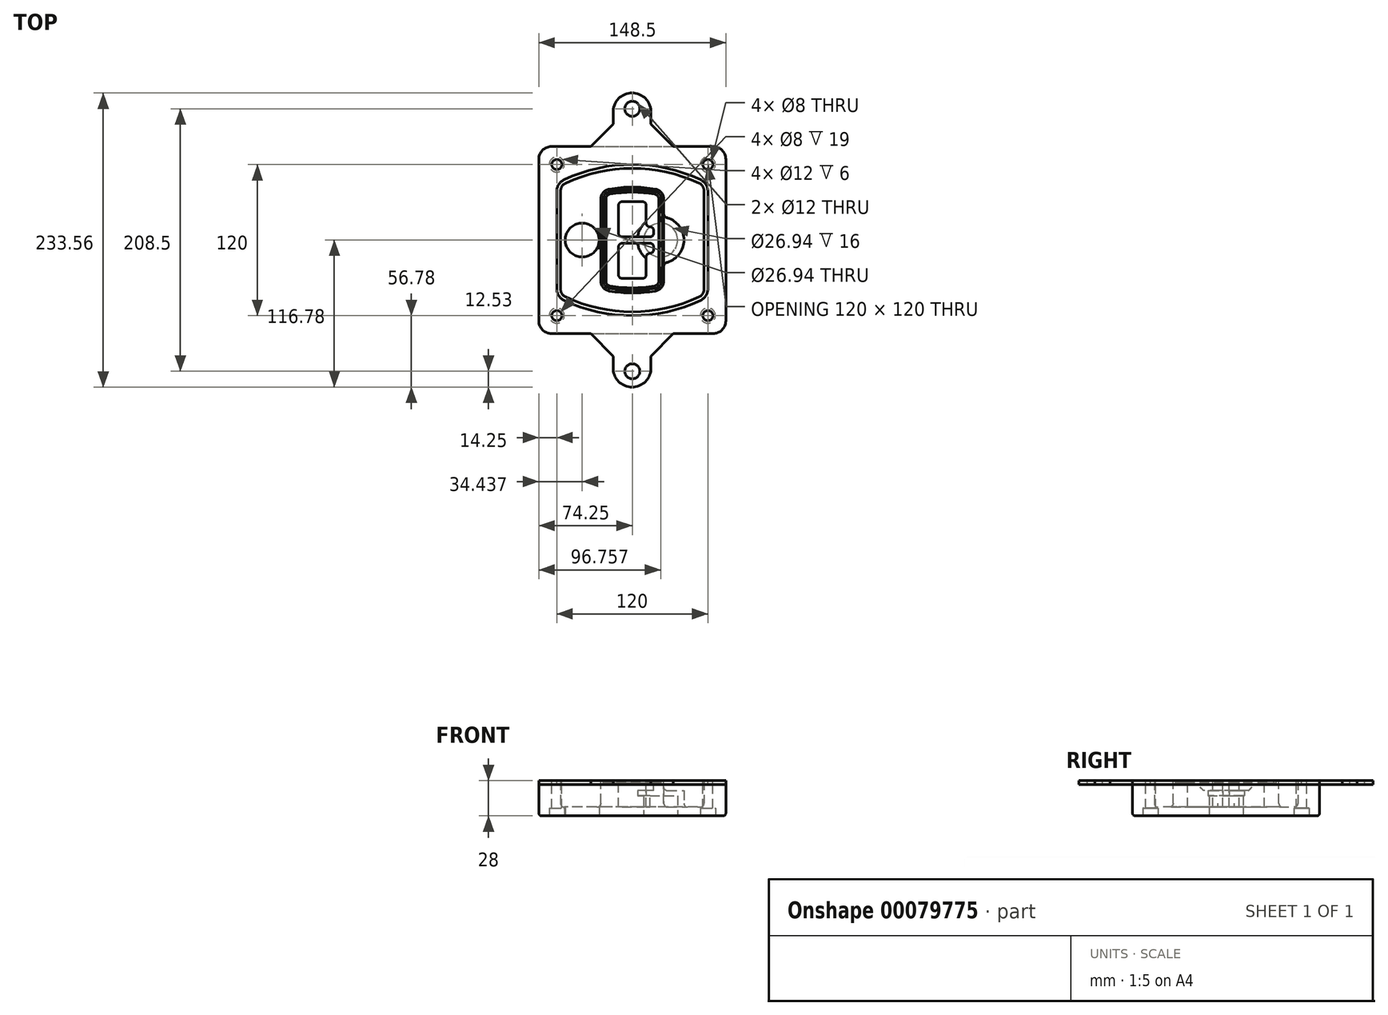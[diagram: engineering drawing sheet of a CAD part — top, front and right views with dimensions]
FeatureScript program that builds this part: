
annotation { "Feature Type Name" : "Feature", "Feature Type Description" : "" }
export const myFeature = defineFeature(function(context is Context, id is Id, definition is map)
    precondition{}
    {
        {
            var Q0;
            Q0=qCreatedBy(makeId("Top.planeOp"),FACE);
            var sketch = newSketch(context, id + "F0", { "sketchPlane" : qUnion([Q0])});
            skPoint(sketch, "E0.rect.middle", {"position": v(0, 0) * mm});
            skLineSegment(sketch, "E1.bottom", {"start": v(-64.25, -74.25) * mm, "end": v(64.25, -74.25) * mm});
            skLineSegment(sketch, "E1.top", {"start": v(-64.25, 74.25) * mm, "end": v(64.25, 74.25) * mm});
            skLineSegment(sketch, "E1.left", {"start": v(-74.25, -64.25) * mm, "end": v(-74.25, 64.25) * mm});
            skLineSegment(sketch, "E1.right", {"start": v(74.25, -64.25) * mm, "end": v(74.25, 64.25) * mm});
            skLineSegment(sketch, "E2", {"start": v(-74.25, 74.25) * mm, "end": v(74.25, -74.25) * mm, "construction": true});
            skLineSegment(sketch, "E3", {"start": v(74.25, 74.25) * mm, "end": v(-74.25, -74.25) * mm, "construction": true});
            skCircle(sketch, "E4", {"center": v(-60, 60) * mm, "radius": 4 * mm});
            skCircle(sketch, "E5", {"center": v(60, 60) * mm, "radius": 4 * mm});
            skCircle(sketch, "E6", {"center": v(60, -60) * mm, "radius": 4 * mm});
            skCircle(sketch, "E7", {"center": v(-60, -60) * mm, "radius": 4 * mm});
            skLineSegment(sketch, "E8", {"start": v(-60, 60) * mm, "end": v(60, 60) * mm, "construction": true});
            skLineSegment(sketch, "E9", {"start": v(60, 60) * mm, "end": v(60, -60) * mm, "construction": true});
            skLineSegment(sketch, "E10", {"start": v(60, -60) * mm, "end": v(-60, -60) * mm, "construction": true});
            skLineSegment(sketch, "E11", {"start": v(-60, -60) * mm, "end": v(-60, 60) * mm, "construction": true});
            skLineSegment(sketch, "E12", {"start": v(-60, 38.83) * mm, "end": v(-60, -38.83) * mm});
            skLineSegment(sketch, "E13", {"start": v(60, 38.83) * mm, "end": v(60, -38.83) * mm});
            skArc(sketch, "E14", {"start": v(54.26, 47.88) * mm, "mid": v(0, 60) * mm, "end": v(-54.26, 47.88) * mm});
            skArc(sketch, "E15", {"start": v(-54.26, -47.88) * mm, "mid": v(0, -60) * mm, "end": v(54.26, -47.88) * mm});
            skLineSegment(sketch, "E16", {"start": v(-60, 0) * mm, "end": v(60, 0) * mm, "construction": true});
            skPoint(sketch, "E17.visualSharp", {"position": v(-60, -45) * mm});
            skArc(sketch, "E17.filletArc", {"start": v(-60, -38.83) * mm, "mid": v(-58.44, -44.2) * mm, "end": v(-54.26, -47.88) * mm});
            skPoint(sketch, "E18.visualSharp", {"position": v(-60, 45) * mm});
            skArc(sketch, "E18.filletArc", {"start": v(-54.26, 47.88) * mm, "mid": v(-58.44, 44.2) * mm, "end": v(-60, 38.83) * mm});
            skPoint(sketch, "E19.visualSharp", {"position": v(60, 45) * mm});
            skArc(sketch, "E19.filletArc", {"start": v(60, 38.83) * mm, "mid": v(58.44, 44.2) * mm, "end": v(54.26, 47.88) * mm});
            skPoint(sketch, "E20.visualSharp", {"position": v(60, -45) * mm});
            skArc(sketch, "E20.filletArc", {"start": v(54.26, -47.88) * mm, "mid": v(58.44, -44.2) * mm, "end": v(60, -38.83) * mm});
            skPoint(sketch, "E21.visualSharp", {"position": v(-74.25, 74.25) * mm});
            skArc(sketch, "E21.filletArc", {"start": v(-64.25, 74.25) * mm, "mid": v(-71.32, 71.32) * mm, "end": v(-74.25, 64.25) * mm});
            skPoint(sketch, "E22.visualSharp", {"position": v(74.25, 74.25) * mm});
            skArc(sketch, "E22.filletArc", {"start": v(74.25, 64.25) * mm, "mid": v(71.32, 71.32) * mm, "end": v(64.25, 74.25) * mm});
            skPoint(sketch, "E23.visualSharp", {"position": v(74.25, -74.25) * mm});
            skArc(sketch, "E23.filletArc", {"start": v(64.25, -74.25) * mm, "mid": v(71.32, -71.32) * mm, "end": v(74.25, -64.25) * mm});
            skPoint(sketch, "E24.visualSharp", {"position": v(-74.25, -74.25) * mm});
            skArc(sketch, "E24.filletArc", {"start": v(-74.25, -64.25) * mm, "mid": v(-71.32, -71.32) * mm, "end": v(-64.25, -74.25) * mm});
            skArc(sketch, "E25.0", {"start": v(57, 38.83) * mm, "mid": v(55.9, 42.58) * mm, "end": v(52.98, 45.17) * mm});
            skLineSegment(sketch, "E25.1", {"start": v(57, 38.83) * mm, "end": v(57, -38.83) * mm});
            skArc(sketch, "E25.2", {"start": v(52.98, -45.17) * mm, "mid": v(55.9, -42.58) * mm, "end": v(57, -38.83) * mm});
            skArc(sketch, "E25.3", {"start": v(-52.98, -45.17) * mm, "mid": v(0, -57) * mm, "end": v(52.98, -45.17) * mm});
            skArc(sketch, "E25.4", {"start": v(-57, -38.83) * mm, "mid": v(-55.9, -42.58) * mm, "end": v(-52.98, -45.17) * mm});
            skArc(sketch, "E25.5", {"start": v(52.98, 45.17) * mm, "mid": v(0, 57) * mm, "end": v(-52.98, 45.17) * mm});
            skLineSegment(sketch, "E25.6", {"start": v(-57, 38.83) * mm, "end": v(-57, -38.83) * mm});
            skArc(sketch, "E25.7", {"start": v(-52.98, 45.17) * mm, "mid": v(-55.9, 42.58) * mm, "end": v(-57, 38.83) * mm});
            skArc(sketch, "E26.0", {"start": v(-55.96, 51.5) * mm, "mid": v(-61.82, 46.33) * mm, "end": v(-64, 38.83) * mm});
            skArc(sketch, "E26.1", {"start": v(55.96, 51.5) * mm, "mid": v(0, 64) * mm, "end": v(-55.96, 51.5) * mm});
            skArc(sketch, "E26.2", {"start": v(64, 38.83) * mm, "mid": v(61.82, 46.33) * mm, "end": v(55.96, 51.5) * mm});
            skLineSegment(sketch, "E26.3", {"start": v(64, 38.83) * mm, "end": v(64, -38.83) * mm});
            skArc(sketch, "E26.4", {"start": v(55.96, -51.5) * mm, "mid": v(61.82, -46.33) * mm, "end": v(64, -38.83) * mm});
            skLineSegment(sketch, "E26.5", {"start": v(-64, 38.83) * mm, "end": v(-64, -38.83) * mm});
            skArc(sketch, "E26.6", {"start": v(-55.96, -51.5) * mm, "mid": v(0, -64) * mm, "end": v(55.96, -51.5) * mm});
            skArc(sketch, "E26.7", {"start": v(-64, -38.83) * mm, "mid": v(-61.82, -46.33) * mm, "end": v(-55.96, -51.5) * mm});
            skSolve(sketch);
        }
        {
            var Q0;
            Q0=makeQuery(id+"F0.imprint","IMPRINT",FACE,{"disambiguationData":[TD([[makeQuery(id+"F0.imprint","IMPRINT",EDGE,{"derivedFrom":sQuery(id+"F0.wireOp",EDGE,"E1.bottom")}),1.0]])]});
            var Q1;
            Q1=makeQuery(id+"F0.imprint","IMPRINT",FACE,{"disambiguationData":[TD([[makeQuery(id+"F0.imprint","IMPRINT",EDGE,{"derivedFrom":sQuery(id+"F0.wireOp",EDGE,"E12")}),1.0]])]});
            var Q2;
            Q2=makeQuery(id+"F0.imprint","IMPRINT",FACE,{"disambiguationData":[TD([[makeQuery(id+"F0.imprint","IMPRINT",EDGE,{"derivedFrom":sQuery(id+"F0.wireOp",EDGE,"E25.0")}),1.0]])]});
            var Q3;
            Q3=makeQuery(id+"F0.imprint","IMPRINT",FACE,{"disambiguationData":[TD([[makeQuery(id+"F0.imprint","IMPRINT",EDGE,{"derivedFrom":sQuery(id+"F0.wireOp",EDGE,"E12")}),-1.0]])]});
            extrude(context, id + "F1", {"entities" : qUnion([Q0, Q1, Q2, Q3]), "oppositeDirection" : true, "depth" : 25 * mm});
        }
        {
            var Q0;
            Q0=makeQuery(id+"F0.imprint","IMPRINT",FACE,{"disambiguationData":[TD([[makeQuery(id+"F0.imprint","IMPRINT",EDGE,{"derivedFrom":sQuery(id+"F0.wireOp",EDGE,"E12")}),1.0]])]});
            extrude(context, id + "F2", {"entities" : qUnion([Q0]), "operationType" : NewBodyOperationType.ADD, "depth" : 3 * mm});
        }
        {
            var Q0;
            Q0=makeQuery(id+"F0.imprint","IMPRINT",FACE,{"disambiguationData":[TD([[makeQuery(id+"F0.imprint","IMPRINT",EDGE,{"derivedFrom":sQuery(id+"F0.wireOp",EDGE,"E25.0")}),1.0]])]});
            extrude(context, id + "F3", {"entities" : qUnion([Q0]), "operationType" : NewBodyOperationType.REMOVE, "oppositeDirection" : true, "depth" : 18 * mm});
        }
        {
            var Q0;
            Q0=makeQuery(id+"F2.opExtrude","CAP_FACE",FACE,{"disambiguationData":[OSD([sQuery(id+"F0.wireOp",EDGE,"E12"),sQuery(id+"F0.wireOp",EDGE,"E13"),sQuery(id+"F0.wireOp",EDGE,"E14"),sQuery(id+"F0.wireOp",EDGE,"E15"),sQuery(id+"F0.wireOp",EDGE,"E17.filletArc"),sQuery(id+"F0.wireOp",EDGE,"E18.filletArc"),sQuery(id+"F0.wireOp",EDGE,"E19.filletArc"),sQuery(id+"F0.wireOp",EDGE,"E20.filletArc"),sQuery(id+"F0.wireOp",EDGE,"E25.0"),sQuery(id+"F0.wireOp",EDGE,"E25.1"),sQuery(id+"F0.wireOp",EDGE,"E25.2"),sQuery(id+"F0.wireOp",EDGE,"E25.3"),sQuery(id+"F0.wireOp",EDGE,"E25.4"),sQuery(id+"F0.wireOp",EDGE,"E25.5"),sQuery(id+"F0.wireOp",EDGE,"E25.6"),sQuery(id+"F0.wireOp",EDGE,"E25.7")])],"isStart":false});
            var sketch = newSketch(context, id + "F4", { "sketchPlane" : qUnion([Q0])});
            skArc(sketch, "E27.0", {"start": v(-18.34, -40.45) * mm, "mid": v(0, -42) * mm, "end": v(18.34, -40.45) * mm});
            skArc(sketch, "E28.0", {"start": v(18.34, 40.45) * mm, "mid": v(0, 42) * mm, "end": v(-18.34, 40.45) * mm});
            skLineSegment(sketch, "E29", {"start": v(-25, 32.57) * mm, "end": v(-25, -32.57) * mm});
            skLineSegment(sketch, "E30", {"start": v(25, 32.57) * mm, "end": v(25, -32.57) * mm});
            skLineSegment(sketch, "E31", {"start": v(-25, 39.1) * mm, "end": v(25, 39.1) * mm, "construction": true});
            skLineSegment(sketch, "E32", {"start": v(-25, -39.1) * mm, "end": v(25, -39.1) * mm, "construction": true});
            skPoint(sketch, "E33.visualSharp", {"position": v(-25, 39.1) * mm});
            skArc(sketch, "E33.filletArc", {"start": v(-18.34, 40.45) * mm, "mid": v(-23.11, 37.73) * mm, "end": v(-25, 32.57) * mm});
            skPoint(sketch, "E34.visualSharp", {"position": v(25, 39.1) * mm});
            skArc(sketch, "E34.filletArc", {"start": v(25, 32.57) * mm, "mid": v(23.11, 37.73) * mm, "end": v(18.34, 40.45) * mm});
            skPoint(sketch, "E35.visualSharp", {"position": v(25, -39.1) * mm});
            skArc(sketch, "E35.filletArc", {"start": v(18.34, -40.45) * mm, "mid": v(23.11, -37.73) * mm, "end": v(25, -32.57) * mm});
            skPoint(sketch, "E36.visualSharp", {"position": v(-25, -39.1) * mm});
            skArc(sketch, "E36.filletArc", {"start": v(-25, -32.57) * mm, "mid": v(-23.11, -37.73) * mm, "end": v(-18.34, -40.45) * mm});
            skArc(sketch, "E37.0", {"start": v(52.98, 45.17) * mm, "mid": v(0, 57) * mm, "end": v(-52.98, 45.17) * mm});
            skArc(sketch, "E37.1", {"start": v(-52.98, 45.17) * mm, "mid": v(-55.9, 42.58) * mm, "end": v(-57, 38.83) * mm});
            skLineSegment(sketch, "E37.2", {"start": v(-57, 38.83) * mm, "end": v(-57, -38.83) * mm});
            skArc(sketch, "E37.3", {"start": v(-57, -38.83) * mm, "mid": v(-55.9, -42.58) * mm, "end": v(-52.98, -45.17) * mm});
            skArc(sketch, "E37.4", {"start": v(-52.98, -45.17) * mm, "mid": v(0, -57) * mm, "end": v(52.98, -45.17) * mm});
            skArc(sketch, "E37.5", {"start": v(52.98, -45.17) * mm, "mid": v(55.9, -42.58) * mm, "end": v(57, -38.83) * mm});
            skLineSegment(sketch, "E37.6", {"start": v(57, 38.83) * mm, "end": v(57, -38.83) * mm});
            skArc(sketch, "E37.7", {"start": v(57, 38.83) * mm, "mid": v(55.9, 42.58) * mm, "end": v(52.98, 45.17) * mm});
            skLineSegment(sketch, "E38.0", {"start": v(23, 32.57) * mm, "end": v(23, -32.57) * mm});
            skArc(sketch, "E38.1", {"start": v(18, -38.48) * mm, "mid": v(21.58, -36.44) * mm, "end": v(23, -32.57) * mm});
            skArc(sketch, "E38.2", {"start": v(-18, -38.48) * mm, "mid": v(0, -40) * mm, "end": v(18, -38.48) * mm});
            skArc(sketch, "E38.3", {"start": v(-23, -32.57) * mm, "mid": v(-21.58, -36.44) * mm, "end": v(-18, -38.48) * mm});
            skLineSegment(sketch, "E38.4", {"start": v(-23, 32.57) * mm, "end": v(-23, -32.57) * mm});
            skArc(sketch, "E38.5", {"start": v(23, 32.57) * mm, "mid": v(21.58, 36.44) * mm, "end": v(18, 38.48) * mm});
            skArc(sketch, "E38.6", {"start": v(-18, 38.48) * mm, "mid": v(-21.58, 36.44) * mm, "end": v(-23, 32.57) * mm});
            skArc(sketch, "E38.7", {"start": v(18, 38.48) * mm, "mid": v(0, 40) * mm, "end": v(-18, 38.48) * mm});
            skArc(sketch, "E39.0", {"start": v(21, 32.57) * mm, "mid": v(20.06, 35.15) * mm, "end": v(17.67, 36.5) * mm});
            skLineSegment(sketch, "E39.1", {"start": v(21, 32.57) * mm, "end": v(21, -32.57) * mm});
            skArc(sketch, "E39.2", {"start": v(17.67, -36.5) * mm, "mid": v(20.06, -35.15) * mm, "end": v(21, -32.57) * mm});
            skArc(sketch, "E39.3", {"start": v(-17.67, -36.5) * mm, "mid": v(0, -38) * mm, "end": v(17.67, -36.5) * mm});
            skArc(sketch, "E39.4", {"start": v(-21, -32.57) * mm, "mid": v(-20.06, -35.15) * mm, "end": v(-17.67, -36.5) * mm});
            skArc(sketch, "E39.5", {"start": v(17.67, 36.5) * mm, "mid": v(0, 38) * mm, "end": v(-17.67, 36.5) * mm});
            skLineSegment(sketch, "E39.6", {"start": v(-21, 32.57) * mm, "end": v(-21, -32.57) * mm});
            skArc(sketch, "E39.7", {"start": v(-17.67, 36.5) * mm, "mid": v(-20.06, 35.15) * mm, "end": v(-21, 32.57) * mm});
            skLineSegment(sketch, "E40", {"start": v(-25, 0) * mm, "end": v(25, 0) * mm, "construction": true});
            skLineSegment(sketch, "E41", {"start": v(-11, 5.5) * mm, "end": v(-11, 27.5) * mm});
            skLineSegment(sketch, "E42", {"start": v(-8, 30.5) * mm, "end": v(8, 30.5) * mm});
            skLineSegment(sketch, "E43", {"start": v(11, 27.5) * mm, "end": v(11, 13.5) * mm});
            skLineSegment(sketch, "E44", {"start": v(14, 10.5) * mm, "end": v(14, 10.5) * mm});
            skLineSegment(sketch, "E45", {"start": v(17, 7.5) * mm, "end": v(17, 5.5) * mm});
            skLineSegment(sketch, "E46", {"start": v(14, 2.5) * mm, "end": v(-8, 2.5) * mm});
            skPoint(sketch, "E47.visualSharp", {"position": v(-11, 30.5) * mm});
            skArc(sketch, "E47.filletArc", {"start": v(-8, 30.5) * mm, "mid": v(-10.12, 29.62) * mm, "end": v(-11, 27.5) * mm});
            skPoint(sketch, "E48.visualSharp", {"position": v(11, 30.5) * mm});
            skArc(sketch, "E48.filletArc", {"start": v(11, 27.5) * mm, "mid": v(10.12, 29.62) * mm, "end": v(8, 30.5) * mm});
            skPoint(sketch, "E49.visualSharp", {"position": v(11, 10.5) * mm});
            skArc(sketch, "E49.filletArc", {"start": v(11, 13.5) * mm, "mid": v(11.88, 11.38) * mm, "end": v(14, 10.5) * mm});
            skPoint(sketch, "E50.visualSharp", {"position": v(17, 10.5) * mm});
            skArc(sketch, "E50.filletArc", {"start": v(17, 7.5) * mm, "mid": v(16.12, 9.62) * mm, "end": v(14, 10.5) * mm});
            skPoint(sketch, "E51.visualSharp", {"position": v(17, 2.5) * mm});
            skArc(sketch, "E51.filletArc", {"start": v(14, 2.5) * mm, "mid": v(16.12, 3.38) * mm, "end": v(17, 5.5) * mm});
            skPoint(sketch, "E52.visualSharp", {"position": v(-11, 2.5) * mm});
            skArc(sketch, "E52.filletArc", {"start": v(-11, 5.5) * mm, "mid": v(-10.12, 3.38) * mm, "end": v(-8, 2.5) * mm});
            skLineSegment(sketch, "E53.0.MirrorCS", {"start": v(14, -2.5) * mm, "end": v(-8, -2.5) * mm});
            skArc(sketch, "E54.0.MirrorCS", {"start": v(-11, -5.5) * mm, "mid": v(-10.12, -3.38) * mm, "end": v(-8, -2.5) * mm});
            skLineSegment(sketch, "E55.0.MirrorCS", {"start": v(-11, -5.5) * mm, "end": v(-11, -27.5) * mm});
            skArc(sketch, "E56.0.MirrorCS", {"start": v(-8, -30.5) * mm, "mid": v(-10.12, -29.62) * mm, "end": v(-11, -27.5) * mm});
            skLineSegment(sketch, "E57.0.MirrorCS", {"start": v(-8, -30.5) * mm, "end": v(8, -30.5) * mm});
            skArc(sketch, "E58.0.MirrorCS", {"start": v(11, -27.5) * mm, "mid": v(10.12, -29.62) * mm, "end": v(8, -30.5) * mm});
            skLineSegment(sketch, "E59.0.MirrorCS", {"start": v(11, -27.5) * mm, "end": v(11, -13.5) * mm});
            skArc(sketch, "E60.0.MirrorCS", {"start": v(11, -13.5) * mm, "mid": v(11.88, -11.38) * mm, "end": v(14, -10.5) * mm});
            skArc(sketch, "E61.0.MirrorCS", {"start": v(17, -7.5) * mm, "mid": v(16.12, -9.62) * mm, "end": v(14, -10.5) * mm});
            skLineSegment(sketch, "E62.0.MirrorCS", {"start": v(17, -7.5) * mm, "end": v(17, -5.5) * mm});
            skArc(sketch, "E63.0.MirrorCS", {"start": v(14, -2.5) * mm, "mid": v(16.12, -3.38) * mm, "end": v(17, -5.5) * mm});
            skSolve(sketch);
        }
        {
            var Q0;
            Q0=makeQuery(id+"F4.imprint","IMPRINT",FACE,{"disambiguationData":[TD([[makeQuery(id+"F4.imprint","IMPRINT",EDGE,{"derivedFrom":sQuery(id+"F4.wireOp",EDGE,"E27.0")}),1.0]])]});
            var Q1;
            Q1=makeQuery(id+"F4.imprint","IMPRINT",FACE,{"disambiguationData":[TD([[makeQuery(id+"F4.imprint","IMPRINT",EDGE,{"derivedFrom":sQuery(id+"F4.wireOp",EDGE,"E38.0")}),-1.0]])]});
            var Q2;
            Q2=makeQuery(id+"F4.imprint","IMPRINT",FACE,{"disambiguationData":[TD([[makeQuery(id+"F4.imprint","IMPRINT",EDGE,{"derivedFrom":sQuery(id+"F4.wireOp",EDGE,"E39.0")}),1.0]])]});
            extrude(context, id + "F5", {"entities" : qUnion([Q0, Q1, Q2]), "operationType" : NewBodyOperationType.ADD, "endBound" : BoundingType.UP_TO_NEXT, "oppositeDirection" : true, "depth" : 25 * mm});
        }
        {
            var Q0;
            Q0=makeQuery(id+"F4.imprint","IMPRINT",FACE,{"disambiguationData":[TD([[makeQuery(id+"F4.imprint","IMPRINT",EDGE,{"derivedFrom":sQuery(id+"F4.wireOp",EDGE,"E38.0")}),-1.0]])]});
            extrude(context, id + "F6", {"entities" : qUnion([Q0]), "operationType" : NewBodyOperationType.REMOVE, "oppositeDirection" : true, "depth" : 2 * mm});
        }
        {
            var Q0;
            Q0=makeQuery(id+"F1.opExtrude","CAP_FACE",FACE,{"disambiguationData":[OSD([sQuery(id+"F0.wireOp",EDGE,"E1.bottom"),sQuery(id+"F0.wireOp",EDGE,"E1.top"),sQuery(id+"F0.wireOp",EDGE,"E1.left"),sQuery(id+"F0.wireOp",EDGE,"E1.right"),sQuery(id+"F0.wireOp",EDGE,"E4"),sQuery(id+"F0.wireOp",EDGE,"E5"),sQuery(id+"F0.wireOp",EDGE,"E6"),sQuery(id+"F0.wireOp",EDGE,"E7"),sQuery(id+"F0.wireOp",EDGE,"E21.filletArc"),sQuery(id+"F0.wireOp",EDGE,"E22.filletArc"),sQuery(id+"F0.wireOp",EDGE,"E23.filletArc"),sQuery(id+"F0.wireOp",EDGE,"E24.filletArc")])],"isStart":false});
            var sketch = newSketch(context, id + "F7", { "sketchPlane" : qUnion([Q0])});
            skCircle(sketch, "E64", {"center": v(22.5, 0) * mm, "radius": 13.47 * mm});
            skCircle(sketch, "E65", {"center": v(-39.81, 0) * mm, "radius": 13.47 * mm});
            skLineSegment(sketch, "E66", {"start": v(74.25, 0) * mm, "end": v(-74.25, 0) * mm});
            skCircle(sketch, "E67", {"center": v(22.5, 0) * mm, "radius": 18.47 * mm});
            skCircle(sketch, "E68", {"center": v(60, -60) * mm, "radius": 6 * mm});
            skCircle(sketch, "E69", {"center": v(-60, -60) * mm, "radius": 6 * mm});
            skCircle(sketch, "E70", {"center": v(-60, 60) * mm, "radius": 6 * mm});
            skCircle(sketch, "E71", {"center": v(60, 60) * mm, "radius": 6 * mm});
            skSolve(sketch);
        }
        {
            var Q0;
            {var subQ1=sQuery(id+"F7.wireOp",EDGE,"E66");var subQ4=sQuery(id+"F7.wireOp",EDGE,"E64");var subQ6=makeQuery(id+"F7.imprint","INTERSECT",VERTEX,{"disambiguationData":[OD(0.0)],"derivedFrom":[subQ4,subQ1]});Q0=makeQuery(id+"F7.imprint","IMPRINT",FACE,{"disambiguationData":[TD([[makeQuery(id+"F7.imprint","IMPRINT",EDGE,{"disambiguationData":[TD([[subQ6,-1.0]])],"derivedFrom":subQ4}),-1.0]])]});}
            var Q1;
            {var subQ0=sQuery(id+"F7.wireOp",EDGE,"E66");var subQ1=sQuery(id+"F7.wireOp",EDGE,"E64");var subQ3=makeQuery(id+"F7.imprint","INTERSECT",VERTEX,{"disambiguationData":[OD(0.0)],"derivedFrom":[subQ1,subQ0]});Q1=makeQuery(id+"F7.imprint","IMPRINT",FACE,{"disambiguationData":[TD([[makeQuery(id+"F7.imprint","IMPRINT",EDGE,{"disambiguationData":[TD([[subQ3,-1.0]])],"derivedFrom":subQ1}),1.0]])]});}
            var Q2;
            {var subQ0=sQuery(id+"F7.wireOp",EDGE,"E66");var subQ1=sQuery(id+"F7.wireOp",EDGE,"E64");var subQ3=makeQuery(id+"F7.imprint","INTERSECT",VERTEX,{"disambiguationData":[OD(0.0)],"derivedFrom":[subQ1,subQ0]});Q2=makeQuery(id+"F7.imprint","IMPRINT",FACE,{"disambiguationData":[TD([[makeQuery(id+"F7.imprint","IMPRINT",EDGE,{"disambiguationData":[TD([[subQ3,1.0]])],"derivedFrom":subQ1}),1.0]])]});}
            var Q3;
            {var subQ1=sQuery(id+"F7.wireOp",EDGE,"E66");var subQ4=sQuery(id+"F7.wireOp",EDGE,"E64");var subQ6=makeQuery(id+"F7.imprint","INTERSECT",VERTEX,{"disambiguationData":[OD(0.0)],"derivedFrom":[subQ4,subQ1]});Q3=makeQuery(id+"F7.imprint","IMPRINT",FACE,{"disambiguationData":[TD([[makeQuery(id+"F7.imprint","IMPRINT",EDGE,{"disambiguationData":[TD([[subQ6,1.0]])],"derivedFrom":subQ4}),-1.0]])]});}
            extrude(context, id + "F8", {"entities" : qUnion([Q0, Q1, Q2, Q3]), "operationType" : NewBodyOperationType.ADD, "oppositeDirection" : true, "depth" : 20 * mm});
        }
        {
            var Q0;
            {var subQ0=sQuery(id+"F7.wireOp",EDGE,"E66");var subQ1=sQuery(id+"F7.wireOp",EDGE,"E64");var subQ3=makeQuery(id+"F7.imprint","INTERSECT",VERTEX,{"disambiguationData":[OD(0.0)],"derivedFrom":[subQ1,subQ0]});Q0=makeQuery(id+"F7.imprint","IMPRINT",FACE,{"disambiguationData":[TD([[makeQuery(id+"F7.imprint","IMPRINT",EDGE,{"disambiguationData":[TD([[subQ3,-1.0]])],"derivedFrom":subQ1}),1.0]])]});}
            var Q1;
            {var subQ0=sQuery(id+"F7.wireOp",EDGE,"E66");var subQ1=sQuery(id+"F7.wireOp",EDGE,"E64");var subQ3=makeQuery(id+"F7.imprint","INTERSECT",VERTEX,{"disambiguationData":[OD(0.0)],"derivedFrom":[subQ1,subQ0]});Q1=makeQuery(id+"F7.imprint","IMPRINT",FACE,{"disambiguationData":[TD([[makeQuery(id+"F7.imprint","IMPRINT",EDGE,{"disambiguationData":[TD([[subQ3,1.0]])],"derivedFrom":subQ1}),1.0]])]});}
            extrude(context, id + "F9", {"entities" : qUnion([Q0, Q1]), "operationType" : NewBodyOperationType.REMOVE, "oppositeDirection" : true, "depth" : 16 * mm});
        }
        {
            var Q0;
            {var subQ0=sQuery(id+"F7.wireOp",EDGE,"E66");var subQ1=sQuery(id+"F7.wireOp",EDGE,"E65");var subQ3=makeQuery(id+"F7.imprint","INTERSECT",VERTEX,{"disambiguationData":[OD(0.0)],"derivedFrom":[subQ1,subQ0]});Q0=makeQuery(id+"F7.imprint","IMPRINT",FACE,{"disambiguationData":[TD([[makeQuery(id+"F7.imprint","IMPRINT",EDGE,{"disambiguationData":[TD([[subQ3,-1.0]])],"derivedFrom":subQ1}),1.0]])]});}
            var Q1;
            {var subQ0=sQuery(id+"F7.wireOp",EDGE,"E66");var subQ1=sQuery(id+"F7.wireOp",EDGE,"E65");var subQ3=makeQuery(id+"F7.imprint","INTERSECT",VERTEX,{"disambiguationData":[OD(0.0)],"derivedFrom":[subQ1,subQ0]});Q1=makeQuery(id+"F7.imprint","IMPRINT",FACE,{"disambiguationData":[TD([[makeQuery(id+"F7.imprint","IMPRINT",EDGE,{"disambiguationData":[TD([[subQ3,1.0]])],"derivedFrom":subQ1}),1.0]])]});}
            extrude(context, id + "F10", {"entities" : qUnion([Q0, Q1]), "operationType" : NewBodyOperationType.REMOVE, "oppositeDirection" : true, "depth" : 25 * mm});
        }
        {
            var Q0;
            Q0=makeQuery(id+"F7.imprint","IMPRINT",FACE,{"disambiguationData":[TD([[makeQuery(id+"F7.imprint","IMPRINT",EDGE,{"derivedFrom":sQuery(id+"F7.wireOp",EDGE,"E68")}),1.0]])]});
            var Q1;
            Q1=makeQuery(id+"F7.imprint","IMPRINT",FACE,{"disambiguationData":[TD([[makeQuery(id+"F7.imprint","IMPRINT",EDGE,{"derivedFrom":makeQuery(id+"F1.opExtrude","CAP_EDGE",EDGE,{"disambiguationData":[OSD([sQuery(id+"F0.wireOp",EDGE,"E5")])],"isStart":false})}),-1.0]])]});
            var Q2;
            Q2=makeQuery(id+"F7.imprint","IMPRINT",FACE,{"disambiguationData":[TD([[makeQuery(id+"F7.imprint","IMPRINT",EDGE,{"derivedFrom":sQuery(id+"F7.wireOp",EDGE,"E69")}),1.0]])]});
            var Q3;
            Q3=makeQuery(id+"F7.imprint","IMPRINT",FACE,{"disambiguationData":[TD([[makeQuery(id+"F7.imprint","IMPRINT",EDGE,{"derivedFrom":makeQuery(id+"F1.opExtrude","CAP_EDGE",EDGE,{"disambiguationData":[OSD([sQuery(id+"F0.wireOp",EDGE,"E4")])],"isStart":false})}),-1.0]])]});
            var Q4;
            Q4=makeQuery(id+"F7.imprint","IMPRINT",FACE,{"disambiguationData":[TD([[makeQuery(id+"F7.imprint","IMPRINT",EDGE,{"derivedFrom":sQuery(id+"F7.wireOp",EDGE,"E70")}),1.0]])]});
            var Q5;
            Q5=makeQuery(id+"F7.imprint","IMPRINT",FACE,{"disambiguationData":[TD([[makeQuery(id+"F7.imprint","IMPRINT",EDGE,{"derivedFrom":makeQuery(id+"F1.opExtrude","CAP_EDGE",EDGE,{"disambiguationData":[OSD([sQuery(id+"F0.wireOp",EDGE,"E7")])],"isStart":false})}),-1.0]])]});
            var Q6;
            Q6=makeQuery(id+"F7.imprint","IMPRINT",FACE,{"disambiguationData":[TD([[makeQuery(id+"F7.imprint","IMPRINT",EDGE,{"derivedFrom":sQuery(id+"F7.wireOp",EDGE,"E71")}),1.0]])]});
            var Q7;
            Q7=makeQuery(id+"F7.imprint","IMPRINT",FACE,{"disambiguationData":[TD([[makeQuery(id+"F7.imprint","IMPRINT",EDGE,{"derivedFrom":makeQuery(id+"F1.opExtrude","CAP_EDGE",EDGE,{"disambiguationData":[OSD([sQuery(id+"F0.wireOp",EDGE,"E6")])],"isStart":false})}),-1.0]])]});
            extrude(context, id + "F11", {"entities" : qUnion([Q0, Q1, Q2, Q3, Q4, Q5, Q6, Q7]), "operationType" : NewBodyOperationType.REMOVE, "oppositeDirection" : true, "depth" : 6 * mm});
        }
        {
            var Q0;
            Q0=makeQuery(id+"F9.boolean.opBoolean","COPY",FACE,{"derivedFrom":makeQuery(id+"F9.opExtrude","CAP_FACE",FACE,{"disambiguationData":[OSD([sQuery(id+"F7.wireOp",EDGE,"E64")])],"isStart":false})});
            var sketch = newSketch(context, id + "F12", { "sketchPlane" : qUnion([Q0])});
            skArc(sketch, "E72.0", {"start": v(11, 14.45) * mm, "mid": v(6.45, 9.13) * mm, "end": v(4.2, 2.5) * mm});
            skArc(sketch, "E72.1", {"start": v(4.2, -2.5) * mm, "mid": v(6.45, -9.13) * mm, "end": v(11, -14.45) * mm});
            skLineSegment(sketch, "E73", {"start": v(4.2, -2.5) * mm, "end": v(14, -2.5) * mm});
            skLineSegment(sketch, "E74.0", {"start": v(14, 2.5) * mm, "end": v(4.2, 2.5) * mm});
            skArc(sketch, "E74.1", {"start": v(14, 2.5) * mm, "mid": v(16.12, 3.38) * mm, "end": v(17, 5.5) * mm});
            skLineSegment(sketch, "E74.2", {"start": v(17, 7.5) * mm, "end": v(17, 5.5) * mm});
            skArc(sketch, "E74.3", {"start": v(17, 7.5) * mm, "mid": v(16.12, 9.62) * mm, "end": v(14, 10.5) * mm});
            skArc(sketch, "E74.4", {"start": v(11, 13.5) * mm, "mid": v(11.88, 11.38) * mm, "end": v(14, 10.5) * mm});
            skLineSegment(sketch, "E74.5", {"start": v(11, 14.45) * mm, "end": v(11, 13.5) * mm});
            skLineSegment(sketch, "E74.7", {"start": v(14, -2.5) * mm, "end": v(4.2, -2.5) * mm});
            skArc(sketch, "E74.8", {"start": v(14, -2.5) * mm, "mid": v(16.12, -3.38) * mm, "end": v(17, -5.5) * mm});
            skLineSegment(sketch, "E74.9", {"start": v(17, -7.5) * mm, "end": v(17, -5.5) * mm});
            skArc(sketch, "E74.10", {"start": v(17, -7.5) * mm, "mid": v(16.12, -9.62) * mm, "end": v(14, -10.5) * mm});
            skArc(sketch, "E74.11", {"start": v(11, -13.5) * mm, "mid": v(11.88, -11.38) * mm, "end": v(14, -10.5) * mm});
            skLineSegment(sketch, "E74.12", {"start": v(11, -14.45) * mm, "end": v(11, -13.5) * mm});
            skPoint(sketch, "E75.orphan", {"position": v(11, -27.5) * mm});
            skPoint(sketch, "E76.orphan", {"position": v(-8, -2.5) * mm});
            skPoint(sketch, "E77.orphan", {"position": v(-8, 2.5) * mm});
            skPoint(sketch, "E78.orphan", {"position": v(11, 27.5) * mm});
            skSolve(sketch);
        }
        {
            var Q0;
            {var subQ7=sQuery(id+"F12.wireOp",EDGE,"E72.0");var subQ14=sQuery(id+"F12.wireOp",EDGE,"E72.1");var subQ16=sQuery(id+"F12.wireOp",EDGE,"E74.1");var subQ18=sQuery(id+"F12.wireOp",EDGE,"E74.8");Q0=qUnion([makeQuery(id+"F12.imprint","IMPRINT",FACE,{"disambiguationData":[TD([[makeQuery(id+"F12.imprint","IMPRINT",EDGE,{"derivedFrom":subQ7}),1.0]])]}),makeQuery(id+"F12.imprint","IMPRINT",FACE,{"disambiguationData":[TD([[makeQuery(id+"F12.imprint","IMPRINT",EDGE,{"derivedFrom":subQ14}),1.0]])]}),makeQuery(id+"F12.imprint","IMPRINT",FACE,{"disambiguationData":[TD([[makeQuery(id+"F12.imprint","IMPRINT",EDGE,{"derivedFrom":subQ16}),1.0]])]}),makeQuery(id+"F12.imprint","IMPRINT",FACE,{"disambiguationData":[TD([[makeQuery(id+"F12.imprint","IMPRINT",EDGE,{"derivedFrom":subQ18}),-1.0]])]})]);}
            var Q1;
            Q1=makeQuery(id+"F5.boolean.opBoolean","SPLIT",FACE,{"disambiguationData":[TD([makeQuery(id+"F5.opExtrude","SWEPT_FACE",FACE,{"disambiguationData":[OSD([sQuery(id+"F4.wireOp",EDGE,"E41")])]})])],"derivedFrom":makeQuery(id+"F3.boolean.opBoolean","COPY",FACE,{"derivedFrom":makeQuery(id+"F3.opExtrude","CAP_FACE",FACE,{"disambiguationData":[OSD([sQuery(id+"F0.wireOp",EDGE,"E25.0"),sQuery(id+"F0.wireOp",EDGE,"E25.1"),sQuery(id+"F0.wireOp",EDGE,"E25.2"),sQuery(id+"F0.wireOp",EDGE,"E25.3"),sQuery(id+"F0.wireOp",EDGE,"E25.4"),sQuery(id+"F0.wireOp",EDGE,"E25.5"),sQuery(id+"F0.wireOp",EDGE,"E25.6"),sQuery(id+"F0.wireOp",EDGE,"E25.7")])],"isStart":false})})});
            extrude(context, id + "F13", {"entities" : qUnion([Q0]), "operationType" : NewBodyOperationType.REMOVE, "endBound" : BoundingType.UP_TO_SURFACE, "endBoundEntityFace" : qUnion([Q1]), "depth" : 25 * mm});
        }
        {
            var Q0;
            Q0=makeQuery(id+"F3.boolean.opBoolean","COPY",EDGE,{"derivedFrom":makeQuery(id+"F3.opExtrude","CAP_EDGE",EDGE,{"disambiguationData":[OSD([sQuery(id+"F0.wireOp",EDGE,"E25.6")])],"isStart":false})});
            var Q1;
            Q1=makeQuery(id+"F8.boolean.opBoolean","INTERSECT",EDGE,{"derivedFrom":[makeQuery(id+"F5.opExtrude","SWEPT_FACE",FACE,{"disambiguationData":[OSD([sQuery(id+"F4.wireOp",EDGE,"E30")])]}),makeQuery(id+"F8.opExtrude","CAP_FACE",FACE,{"disambiguationData":[OSD([sQuery(id+"F7.wireOp",EDGE,"E67")])],"isStart":false})]});
            var Q2;
            Q2=makeQuery(id+"F8.boolean.opBoolean","INTERSECT",EDGE,{"disambiguationData":[OD(1.0)],"derivedFrom":[makeQuery(id+"F5.opExtrude","SWEPT_FACE",FACE,{"disambiguationData":[OSD([sQuery(id+"F4.wireOp",EDGE,"E30")])]}),makeQuery(id+"F8.opExtrude","SWEPT_FACE",FACE,{"disambiguationData":[OSD([sQuery(id+"F7.wireOp",EDGE,"E67")])]})]});
            var Q3;
            {var subQ0=sQuery(id+"F4.wireOp",EDGE,"E30");Q3=makeQuery(id+"F8.boolean.opBoolean","SPLIT",EDGE,{"disambiguationData":[TD([makeQuery(id+"F5.opExtrude","SWEPT_FACE",FACE,{"disambiguationData":[OSD([sQuery(id+"F4.wireOp",EDGE,"E35.filletArc")])]})])],"derivedFrom":makeQuery(id+"F5.opExtrude","CAP_EDGE",EDGE,{"disambiguationData":[OSD([subQ0])],"isStart":false})});}
            var Q4;
            {var subQ0=sQuery(id+"F0.wireOp",EDGE,"E25.7");var subQ1=sQuery(id+"F0.wireOp",EDGE,"E25.1");var subQ2=sQuery(id+"F0.wireOp",EDGE,"E25.6");var subQ3=sQuery(id+"F0.wireOp",EDGE,"E25.5");var subQ4=sQuery(id+"F0.wireOp",EDGE,"E25.4");var subQ5=sQuery(id+"F0.wireOp",EDGE,"E25.0");var subQ6=sQuery(id+"F0.wireOp",EDGE,"E25.2");var subQ7=sQuery(id+"F0.wireOp",EDGE,"E25.3");Q4=makeQuery(id+"F8.boolean.opBoolean","INTERSECT",EDGE,{"derivedFrom":[makeQuery(id+"F5.boolean.opBoolean","SPLIT",FACE,{"disambiguationData":[TD([makeQuery(id+"F2.opExtrude","SWEPT_FACE",FACE,{"disambiguationData":[OSD([subQ5])]})])],"derivedFrom":makeQuery(id+"F3.boolean.opBoolean","COPY",FACE,{"derivedFrom":makeQuery(id+"F3.opExtrude","CAP_FACE",FACE,{"disambiguationData":[OSD([subQ5,subQ1,subQ6,subQ7,subQ4,subQ3,subQ2,subQ0])],"isStart":false})})}),makeQuery(id+"F8.opExtrude","SWEPT_FACE",FACE,{"disambiguationData":[OSD([sQuery(id+"F7.wireOp",EDGE,"E67")])]})]});}
            var Q5;
            Q5=makeQuery(id+"F8.boolean.opBoolean","INTERSECT",EDGE,{"disambiguationData":[OD(0.0)],"derivedFrom":[makeQuery(id+"F5.opExtrude","SWEPT_FACE",FACE,{"disambiguationData":[OSD([sQuery(id+"F4.wireOp",EDGE,"E30")])]}),makeQuery(id+"F8.opExtrude","SWEPT_FACE",FACE,{"disambiguationData":[OSD([sQuery(id+"F7.wireOp",EDGE,"E67")])]})]});
            fillet(context, id + "F14", {"entities" : qUnion([Q0, Q1, Q2, Q3, Q4, Q5]), "radius" : 3 * mm, "tangentPropagation" : true, "allowEdgeOverflow" : false});
        }
        {
            var Q0;
            Q0=makeQuery(id+"F1.opExtrude","CAP_EDGE",EDGE,{"disambiguationData":[OSD([sQuery(id+"F0.wireOp",EDGE,"E1.bottom")])],"isStart":false});
            fillet(context, id + "F15", {"entities" : qUnion([Q0]), "radius" : 2 * mm, "tangentPropagation" : true, "allowEdgeOverflow" : false});
        }
        {
            var Q0;
            Q0=makeQuery(id+"F2.opExtrude","CAP_FACE",FACE,{"disambiguationData":[OSD([sQuery(id+"F0.wireOp",EDGE,"E12"),sQuery(id+"F0.wireOp",EDGE,"E13"),sQuery(id+"F0.wireOp",EDGE,"E14"),sQuery(id+"F0.wireOp",EDGE,"E15"),sQuery(id+"F0.wireOp",EDGE,"E17.filletArc"),sQuery(id+"F0.wireOp",EDGE,"E18.filletArc"),sQuery(id+"F0.wireOp",EDGE,"E19.filletArc"),sQuery(id+"F0.wireOp",EDGE,"E20.filletArc"),sQuery(id+"F0.wireOp",EDGE,"E25.0"),sQuery(id+"F0.wireOp",EDGE,"E25.1"),sQuery(id+"F0.wireOp",EDGE,"E25.2"),sQuery(id+"F0.wireOp",EDGE,"E25.3"),sQuery(id+"F0.wireOp",EDGE,"E25.4"),sQuery(id+"F0.wireOp",EDGE,"E25.5"),sQuery(id+"F0.wireOp",EDGE,"E25.6"),sQuery(id+"F0.wireOp",EDGE,"E25.7")])],"isStart":false});
            var sketch = newSketch(context, id + "F16", { "sketchPlane" : qUnion([Q0])});
            skArc(sketch, "E79.0", {"start": v(54.26, 47.88) * mm, "mid": v(0, 60) * mm, "end": v(-54.26, 47.88) * mm});
            skArc(sketch, "E79.1", {"start": v(-54.26, 47.88) * mm, "mid": v(-58.44, 44.2) * mm, "end": v(-60, 38.83) * mm});
            skLineSegment(sketch, "E79.2", {"start": v(-60, 38.83) * mm, "end": v(-60, -38.83) * mm});
            skArc(sketch, "E79.3", {"start": v(-60, -38.83) * mm, "mid": v(-58.44, -44.2) * mm, "end": v(-54.26, -47.88) * mm});
            skArc(sketch, "E79.4", {"start": v(-54.26, -47.88) * mm, "mid": v(0, -60) * mm, "end": v(54.26, -47.88) * mm});
            skArc(sketch, "E79.5", {"start": v(54.26, -47.88) * mm, "mid": v(58.44, -44.2) * mm, "end": v(60, -38.83) * mm});
            skLineSegment(sketch, "E79.6", {"start": v(60, 38.83) * mm, "end": v(60, -38.83) * mm});
            skArc(sketch, "E79.7", {"start": v(60, 38.83) * mm, "mid": v(58.44, 44.2) * mm, "end": v(54.26, 47.88) * mm});
            skCircle(sketch, "E79.8", {"center": v(60, 60) * mm, "radius": 4 * mm});
            skCircle(sketch, "E79.9", {"center": v(60, -60) * mm, "radius": 4 * mm});
            skCircle(sketch, "E79.10", {"center": v(-60, -60) * mm, "radius": 4 * mm});
            skCircle(sketch, "E79.11", {"center": v(-60, 60) * mm, "radius": 4 * mm});
            skLineSegment(sketch, "E79.12", {"start": v(-64.25, 74.25) * mm, "end": v(64.25, 74.25) * mm});
            skArc(sketch, "E79.13", {"start": v(-64.25, 74.25) * mm, "mid": v(-71.32, 71.32) * mm, "end": v(-74.25, 64.25) * mm});
            skLineSegment(sketch, "E79.14", {"start": v(-74.25, -64.25) * mm, "end": v(-74.25, 64.25) * mm});
            skArc(sketch, "E79.15", {"start": v(-74.25, -64.25) * mm, "mid": v(-71.32, -71.32) * mm, "end": v(-64.25, -74.25) * mm});
            skLineSegment(sketch, "E79.16", {"start": v(-64.25, -74.25) * mm, "end": v(64.25, -74.25) * mm});
            skArc(sketch, "E79.17", {"start": v(64.25, -74.25) * mm, "mid": v(71.32, -71.32) * mm, "end": v(74.25, -64.25) * mm});
            skArc(sketch, "E79.18", {"start": v(74.25, 64.25) * mm, "mid": v(71.32, 71.32) * mm, "end": v(64.25, 74.25) * mm});
            skLineSegment(sketch, "E79.19", {"start": v(74.25, -64.25) * mm, "end": v(74.25, 64.25) * mm, "construction": true});
            skLineSegment(sketch, "E80", {"start": v(0, 104.25) * mm, "end": v(0, 74.25) * mm, "construction": true});
            skArc(sketch, "E81", {"start": v(14.6, 104.25) * mm, "mid": v(-0.2, 116.78) * mm, "end": v(-15, 104.25) * mm});
            skCircle(sketch, "E82", {"center": v(0, 104.25) * mm, "radius": 6 * mm});
            skLineSegment(sketch, "E83", {"start": v(14.6, 104.25) * mm, "end": v(14.6, 92.25) * mm});
            skLineSegment(sketch, "E84", {"start": v(-15, 104.25) * mm, "end": v(-15, 92.25) * mm});
            skLineSegment(sketch, "E85", {"start": v(14.6, 92.25) * mm, "end": v(32.6, 74.25) * mm});
            skLineSegment(sketch, "E86", {"start": v(-15, 92.25) * mm, "end": v(-33, 74.25) * mm});
            skLineSegment(sketch, "E87", {"start": v(74.25, 64.25) * mm, "end": v(74.25, -64.25) * mm});
            skLineSegment(sketch, "E88", {"start": v(-74.25, 0) * mm, "end": v(74.25, 0) * mm, "construction": true});
            skLineSegment(sketch, "E89", {"start": v(-33, 74.25) * mm, "end": v(32.6, 74.25) * mm});
            skCircle(sketch, "E90.MirrorC", {"center": v(0, -104.25) * mm, "radius": 6 * mm});
            skLineSegment(sketch, "E91.MirrorCS", {"start": v(-15, -104.25) * mm, "end": v(-15, -92.25) * mm});
            skArc(sketch, "E92.MirrorCS", {"start": v(14.6, -104.25) * mm, "mid": v(-0.2, -116.78) * mm, "end": v(-15, -104.25) * mm});
            skLineSegment(sketch, "E93.MirrorCS", {"start": v(14.6, -104.25) * mm, "end": v(14.6, -92.25) * mm});
            skLineSegment(sketch, "E94.MirrorCS", {"start": v(14.6, -92.25) * mm, "end": v(32.6, -74.25) * mm});
            skLineSegment(sketch, "E95.MirrorCS", {"start": v(-33, -74.25) * mm, "end": v(32.6, -74.25) * mm});
            skLineSegment(sketch, "E96.MirrorCS", {"start": v(-15, -92.25) * mm, "end": v(-33, -74.25) * mm});
            skSolve(sketch);
        }
        {
            var Q0;
            Q0 = qSketchRegion(id + "F16", true);
            var Q1;
            {var subQ0=sQuery(id+"F0.wireOp",EDGE,"E22.filletArc");var subQ1=sQuery(id+"F0.wireOp",EDGE,"E7");var subQ2=sQuery(id+"F0.wireOp",EDGE,"E6");var subQ3=sQuery(id+"F0.wireOp",EDGE,"E5");var subQ4=sQuery(id+"F0.wireOp",EDGE,"E4");var subQ5=sQuery(id+"F0.wireOp",EDGE,"E1.bottom");var subQ6=sQuery(id+"F0.wireOp",EDGE,"E21.filletArc");var subQ7=sQuery(id+"F0.wireOp",EDGE,"E1.top");var subQ8=sQuery(id+"F0.wireOp",EDGE,"E1.left");var subQ9=sQuery(id+"F0.wireOp",EDGE,"E1.right");var subQ10=sQuery(id+"F0.wireOp",EDGE,"E23.filletArc");var subQ11=sQuery(id+"F0.wireOp",EDGE,"E24.filletArc");Q1=makeQuery(id+"F2.boolean.opBoolean","SPLIT",FACE,{"disambiguationData":[TD([makeQuery(id+"F1.opExtrude","SWEPT_FACE",FACE,{"disambiguationData":[OSD([subQ5])]})])],"derivedFrom":makeQuery(id+"F1.opExtrude","CAP_FACE",FACE,{"disambiguationData":[OSD([subQ5,subQ7,subQ8,subQ9,subQ4,subQ3,subQ2,subQ1,subQ6,subQ0,subQ10,subQ11])],"isStart":true})});}
            extrude(context, id + "F17", {"entities" : qUnion([Q0]), "endBound" : BoundingType.UP_TO_SURFACE, "oppositeDirection" : true, "endBoundEntityFace" : qUnion([Q1]), "depth" : 1.48 * mm});
        }
    });
